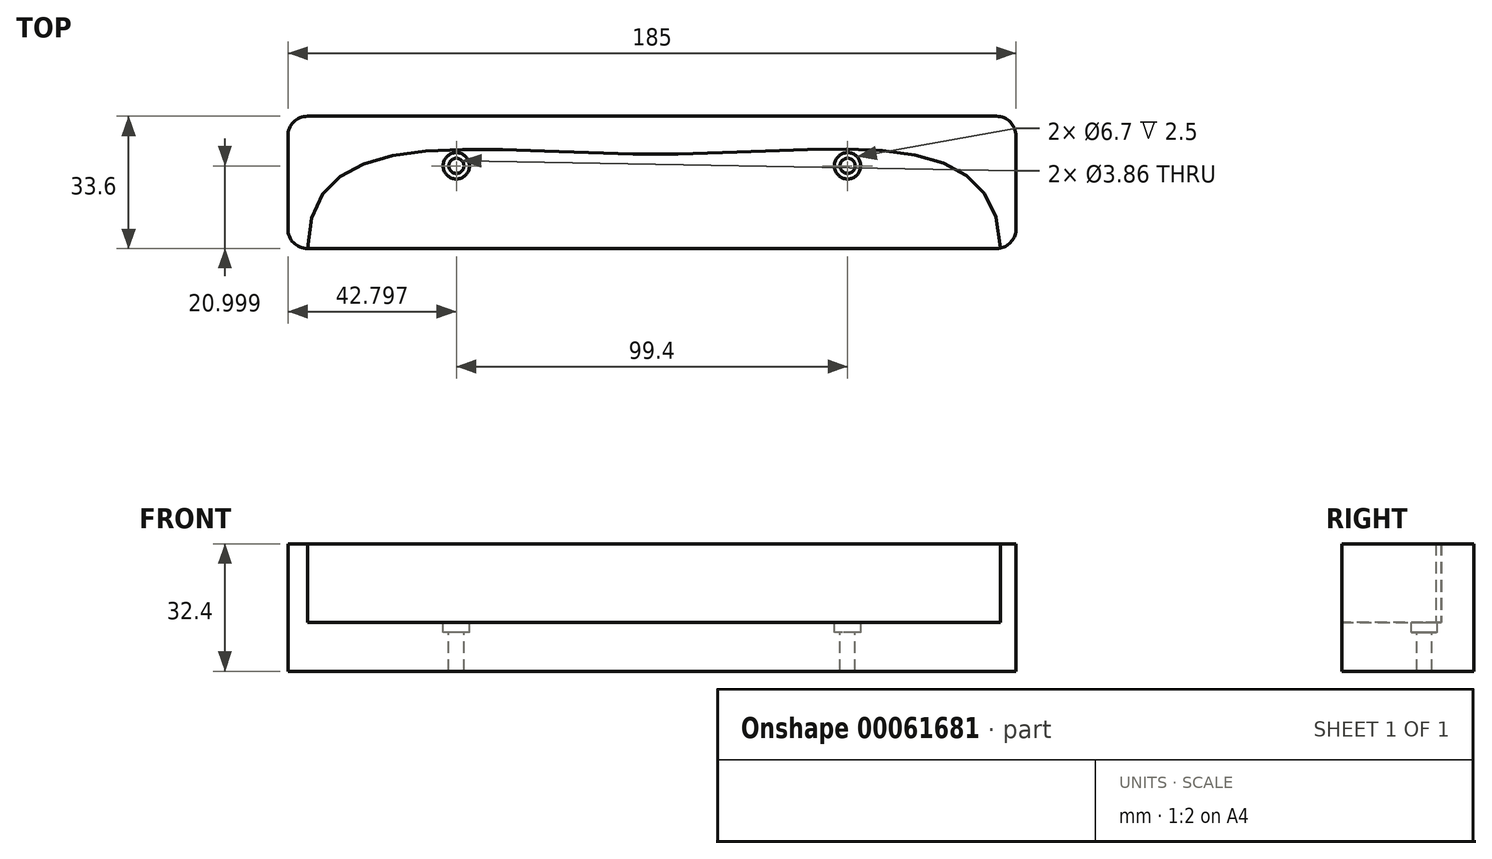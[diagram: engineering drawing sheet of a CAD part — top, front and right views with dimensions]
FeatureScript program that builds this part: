
annotation { "Feature Type Name" : "Feature", "Feature Type Description" : "" }
export const myFeature = defineFeature(function(context is Context, id is Id, definition is map)
    precondition{}
    {
        {
            var Q0;
            Q0=qCreatedBy(makeId("Top.planeOp"),FACE);
            var sketch = newSketch(context, id + "F0", { "sketchPlane" : qUnion([Q0])});
            skLineSegment(sketch, "E0.bottom", {"start": v(-89.36, -7.5) * mm, "end": v(85.64, -7.5) * mm});
            skLineSegment(sketch, "E0.top", {"start": v(-89.36, -41.1) * mm, "end": v(85.64, -41.1) * mm});
            skLineSegment(sketch, "E0.left", {"start": v(-94.36, -12.5) * mm, "end": v(-94.36, -36.1) * mm});
            skLineSegment(sketch, "E0.right", {"start": v(90.64, -12.5) * mm, "end": v(90.64, -36.1) * mm});
            skPoint(sketch, "E1.visualSharp", {"position": v(-94.36, -7.5) * mm});
            skArc(sketch, "E1.filletArc", {"start": v(-89.36, -7.5) * mm, "mid": v(-92.9, -8.97) * mm, "end": v(-94.36, -12.5) * mm});
            skPoint(sketch, "E2.visualSharp", {"position": v(-94.36, -41.1) * mm});
            skArc(sketch, "E2.filletArc", {"start": v(-94.36, -36.1) * mm, "mid": v(-92.9, -39.64) * mm, "end": v(-89.36, -41.1) * mm});
            skPoint(sketch, "E3.visualSharp", {"position": v(90.64, -41.1) * mm});
            skArc(sketch, "E3.filletArc", {"start": v(85.64, -41.1) * mm, "mid": v(89.17, -39.64) * mm, "end": v(90.64, -36.1) * mm});
            skPoint(sketch, "E4.visualSharp", {"position": v(90.64, -7.5) * mm});
            skArc(sketch, "E4.filletArc", {"start": v(90.64, -12.5) * mm, "mid": v(89.17, -8.97) * mm, "end": v(85.64, -7.5) * mm});
            skFitSpline(sketch, "E5", {"points": [v(-89.36, -41.1) * mm, v(0, -18.1) * mm, v(85.64, -41.1) * mm], "startDerivative": vector(177.84, 38.38) * mm, "endDerivative": vector(172.14, -38.64) * mm});
            skSolve(sketch);
        }
        {
            var Q0;
            {var subQ6=sQuery(id+"F0.wireOp",EDGE,"E0.left");Q0=makeQuery(id+"F0.imprint","IMPRINT",FACE,{"disambiguationData":[TD([[makeQuery(id+"F0.imprint","IMPRINT",EDGE,{"derivedFrom":subQ6}),1.0]])]});}
            var Q1;
            {var subQ0=sQuery(id+"F0.wireOp",EDGE,"E2.filletArc");var subQ1=sQuery(id+"F0.wireOp",EDGE,"E0.top");var subQ2=makeQuery(id+"F0.imprint","INTERSECT",VERTEX,{"derivedFrom":[subQ1,subQ0]});Q1=makeQuery(id+"F0.imprint","IMPRINT",FACE,{"disambiguationData":[TD([[makeQuery(id+"F0.imprint","IMPRINT",EDGE,{"disambiguationData":[TD([[subQ2,-1.0]])],"derivedFrom":subQ1}),1.0]])]});}
            var Q2;
            {var subQ5=sQuery(id+"F0.wireOp",EDGE,"DiWK0a0K-p0Ve-xPCM-Xpb8-uTkeJafHcErU");Q2=makeQuery(id+"F0.imprint","IMPRINT",FACE,{"disambiguationData":[TD([[makeQuery(id+"F0.imprint","IMPRINT",EDGE,{"derivedFrom":subQ5}),1.0]])]});}
            var Q3;
            {var subQ0=sQuery(id+"F0.wireOp",EDGE,"XpN96RJf-h1wa-usSg-oxlj-EXDZ94Ahnvhv");var subQ1=sQuery(id+"F0.wireOp",EDGE,"E0.top");var subQ2=makeQuery(id+"F0.imprint","INTERSECT",VERTEX,{"derivedFrom":[subQ1,subQ0]});Q3=makeQuery(id+"F0.imprint","IMPRINT",FACE,{"disambiguationData":[TD([[makeQuery(id+"F0.imprint","IMPRINT",EDGE,{"disambiguationData":[TD([[subQ2,1.0]])],"derivedFrom":subQ1}),1.0]])]});}
            var Q4;
            {var subQ5=sQuery(id+"F0.wireOp",EDGE,"Qj6dQj5D-QQnR-hAFS-0dMR-JZPYQxWabMse");Q4=makeQuery(id+"F0.imprint","IMPRINT",FACE,{"disambiguationData":[TD([[makeQuery(id+"F0.imprint","IMPRINT",EDGE,{"derivedFrom":subQ5}),-1.0]])]});}
            var Q5;
            {var subQ9=sQuery(id+"F0.wireOp",EDGE,"E0.right");Q5=makeQuery(id+"F0.imprint","IMPRINT",FACE,{"disambiguationData":[TD([[makeQuery(id+"F0.imprint","IMPRINT",EDGE,{"derivedFrom":subQ9}),-1.0]])]});}
            var Q6;
            {var subQ0=sQuery(id+"F0.wireOp",EDGE,"E3.filletArc");var subQ1=sQuery(id+"F0.wireOp",EDGE,"E0.top");var subQ2=makeQuery(id+"F0.imprint","INTERSECT",VERTEX,{"derivedFrom":[subQ1,subQ0]});Q6=makeQuery(id+"F0.imprint","IMPRINT",FACE,{"disambiguationData":[TD([[makeQuery(id+"F0.imprint","IMPRINT",EDGE,{"disambiguationData":[TD([[subQ2,1.0]])],"derivedFrom":subQ1}),1.0]])]});}
            var Q7;
            {var subQ0=sQuery(id+"F0.wireOp",EDGE,"8f524986-9a2f-477d-a438-1098895b14b8");var subQ1=sQuery(id+"F0.wireOp",EDGE,"q3M1eQDT-CZSL-Hfhw-1e6b-vYKe8UV4ZBwo");var subQ2=makeQuery(id+"F0.imprint","INTERSECT",VERTEX,{"disambiguationData":[OD(0.0)],"derivedFrom":[subQ1,subQ0]});Q7=makeQuery(id+"F0.imprint","IMPRINT",FACE,{"disambiguationData":[TD([[makeQuery(id+"F0.imprint","IMPRINT",EDGE,{"disambiguationData":[TD([[subQ2,-1.0]])],"derivedFrom":subQ1}),1.0]])]});}
            var Q8;
            {var subQ0=sQuery(id+"F0.wireOp",EDGE,"f629a123-b092-4783-abd5-7fa05e799837");var subQ1=sQuery(id+"F0.wireOp",EDGE,"q3M1eQDT-CZSL-Hfhw-1e6b-vYKe8UV4ZBwo");var subQ2=makeQuery(id+"F0.imprint","INTERSECT",VERTEX,{"disambiguationData":[OD(0.0)],"derivedFrom":[subQ1,subQ0]});Q8=makeQuery(id+"F0.imprint","IMPRINT",FACE,{"disambiguationData":[TD([[makeQuery(id+"F0.imprint","IMPRINT",EDGE,{"disambiguationData":[TD([[subQ2,-1.0]])],"derivedFrom":subQ1}),1.0]])]});}
            var Q9;
            {var subQ0=sQuery(id+"F0.wireOp",EDGE,"f629a123-b092-4783-abd5-7fa05e799837");var subQ1=sQuery(id+"F0.wireOp",EDGE,"q3M1eQDT-CZSL-Hfhw-1e6b-vYKe8UV4ZBwo");var subQ2=makeQuery(id+"F0.imprint","INTERSECT",VERTEX,{"disambiguationData":[OD(0.0)],"derivedFrom":[subQ1,subQ0]});Q9=makeQuery(id+"F0.imprint","IMPRINT",FACE,{"disambiguationData":[TD([[makeQuery(id+"F0.imprint","IMPRINT",EDGE,{"disambiguationData":[TD([[subQ2,-1.0]])],"derivedFrom":subQ1}),-1.0]])]});}
            var Q10;
            {var subQ0=sQuery(id+"F0.wireOp",EDGE,"8f524986-9a2f-477d-a438-1098895b14b8");var subQ1=sQuery(id+"F0.wireOp",EDGE,"q3M1eQDT-CZSL-Hfhw-1e6b-vYKe8UV4ZBwo");var subQ2=makeQuery(id+"F0.imprint","INTERSECT",VERTEX,{"disambiguationData":[OD(0.0)],"derivedFrom":[subQ1,subQ0]});Q10=makeQuery(id+"F0.imprint","IMPRINT",FACE,{"disambiguationData":[TD([[makeQuery(id+"F0.imprint","IMPRINT",EDGE,{"disambiguationData":[TD([[subQ2,-1.0]])],"derivedFrom":subQ1}),-1.0]])]});}
            var Q11;
            {var subQ0=sQuery(id+"F0.wireOp",EDGE,"e7c36ffa-8dd1-4ad2-a08c-114cf6db0365");var subQ1=sQuery(id+"F0.wireOp",EDGE,"NGp6TUnh-2WYz-SvJ6-BtMD-nmsAgSWZyCNH");var subQ2=makeQuery(id+"F0.imprint","INTERSECT",VERTEX,{"disambiguationData":[OD(0.0)],"derivedFrom":[subQ1,subQ0]});Q11=makeQuery(id+"F0.imprint","IMPRINT",FACE,{"disambiguationData":[TD([[makeQuery(id+"F0.imprint","IMPRINT",EDGE,{"disambiguationData":[TD([[subQ2,-1.0]])],"derivedFrom":subQ1}),1.0]])]});}
            var Q12;
            {var subQ0=sQuery(id+"F0.wireOp",EDGE,"e7c36ffa-8dd1-4ad2-a08c-114cf6db0365");var subQ1=sQuery(id+"F0.wireOp",EDGE,"NGp6TUnh-2WYz-SvJ6-BtMD-nmsAgSWZyCNH");var subQ2=makeQuery(id+"F0.imprint","INTERSECT",VERTEX,{"disambiguationData":[OD(0.0)],"derivedFrom":[subQ1,subQ0]});Q12=makeQuery(id+"F0.imprint","IMPRINT",FACE,{"disambiguationData":[TD([[makeQuery(id+"F0.imprint","IMPRINT",EDGE,{"disambiguationData":[TD([[subQ2,-1.0]])],"derivedFrom":subQ1}),-1.0]])]});}
            var Q13;
            {var subQ0=sQuery(id+"F0.wireOp",EDGE,"635bec6d-890f-4d85-b6bb-3d27c9027523");var subQ1=sQuery(id+"F0.wireOp",EDGE,"NGp6TUnh-2WYz-SvJ6-BtMD-nmsAgSWZyCNH");var subQ2=makeQuery(id+"F0.imprint","INTERSECT",VERTEX,{"disambiguationData":[OD(0.0)],"derivedFrom":[subQ1,subQ0]});Q13=makeQuery(id+"F0.imprint","IMPRINT",FACE,{"disambiguationData":[TD([[makeQuery(id+"F0.imprint","IMPRINT",EDGE,{"disambiguationData":[TD([[subQ2,-1.0]])],"derivedFrom":subQ1}),-1.0]])]});}
            var Q14;
            {var subQ0=sQuery(id+"F0.wireOp",EDGE,"635bec6d-890f-4d85-b6bb-3d27c9027523");var subQ1=sQuery(id+"F0.wireOp",EDGE,"NGp6TUnh-2WYz-SvJ6-BtMD-nmsAgSWZyCNH");var subQ2=makeQuery(id+"F0.imprint","INTERSECT",VERTEX,{"disambiguationData":[OD(0.0)],"derivedFrom":[subQ1,subQ0]});Q14=makeQuery(id+"F0.imprint","IMPRINT",FACE,{"disambiguationData":[TD([[makeQuery(id+"F0.imprint","IMPRINT",EDGE,{"disambiguationData":[TD([[subQ2,-1.0]])],"derivedFrom":subQ1}),1.0]])]});}
            var Q15;
            {var subQ0=sQuery(id+"F0.wireOp",EDGE,"XpN96RJf-h1wa-usSg-oxlj-EXDZ94Ahnvhv");var subQ1=sQuery(id+"F0.wireOp",EDGE,"E0.top");var subQ2=makeQuery(id+"F0.imprint","INTERSECT",VERTEX,{"derivedFrom":[subQ1,subQ0]});Q15=makeQuery(id+"F0.imprint","IMPRINT",FACE,{"disambiguationData":[TD([[makeQuery(id+"F0.imprint","IMPRINT",EDGE,{"disambiguationData":[TD([[subQ2,-1.0]])],"derivedFrom":subQ1}),1.0]])]});}
            extrude(context, id + "F1", {"entities" : qUnion([Q0, Q1, Q2, Q3, Q4, Q5, Q6, Q7, Q8, Q9, Q10, Q11, Q12, Q13, Q14, Q15]), "depth" : 32.4 * mm});
        }
        {
            var Q0;
            Q0=makeQuery(id+"F1.opExtrude","CAP_FACE",FACE,{"disambiguationData":[OSD([sQuery(id+"F0.wireOp",EDGE,"E0.bottom"),sQuery(id+"F0.wireOp",EDGE,"E0.top"),sQuery(id+"F0.wireOp",EDGE,"E0.left"),sQuery(id+"F0.wireOp",EDGE,"E0.right"),sQuery(id+"F0.wireOp",EDGE,"E1.filletArc"),sQuery(id+"F0.wireOp",EDGE,"E2.filletArc"),sQuery(id+"F0.wireOp",EDGE,"E3.filletArc"),sQuery(id+"F0.wireOp",EDGE,"E4.filletArc")])],"isStart":false});
            var sketch = newSketch(context, id + "F2", { "sketchPlane" : qUnion([Q0])});
            skFitSpline(sketch, "E6", {"points": [v(-89.36, -41.1) * mm, v(0, -17.14) * mm, v(86.67, -41) * mm], "startDerivative": vector(0, 200.16) * mm, "endDerivative": vector(6.27, -202.4) * mm});
            skSolve(sketch);
        }
        {
            var Q0;
            {var subQ0=sQuery(id+"F2.wireOp",EDGE,"E6");Q0=makeQuery(id+"F2.imprint","IMPRINT",FACE,{"disambiguationData":[TD([[makeQuery(id+"F2.imprint","IMPRINT",EDGE,{"derivedFrom":subQ0}),-1.0]])]});}
            extrude(context, id + "F3", {"entities" : qUnion([Q0]), "operationType" : NewBodyOperationType.REMOVE, "oppositeDirection" : true, "depth" : 20 * mm});
        }
        {
            var Q0;
            Q0=makeQuery(id+"F3.boolean.opBoolean","COPY",FACE,{"derivedFrom":makeQuery(id+"F3.opExtrude","CAP_FACE",FACE,{"disambiguationData":[OSD([sQuery(id+"F0.wireOp",EDGE,"E0.top"),sQuery(id+"F0.wireOp",EDGE,"E3.filletArc"),sQuery(id+"F2.wireOp",EDGE,"E6")])],"isStart":false})});
            var sketch = newSketch(context, id + "F4", { "sketchPlane" : qUnion([Q0])});
            skLineSegment(sketch, "E7", {"start": v(-1.86, -41.1) * mm, "end": v(-1.86, -20.1) * mm});
            skLineSegment(sketch, "E8", {"start": v(-1.86, -20.1) * mm, "end": v(-51.56, -20.1) * mm});
            skLineSegment(sketch, "E9", {"start": v(-1.86, -20.1) * mm, "end": v(47.84, -20.1) * mm});
            skCircle(sketch, "E10", {"center": v(-51.56, -20.1) * mm, "radius": 3.35 * mm});
            skCircle(sketch, "E11", {"center": v(47.84, -20.1) * mm, "radius": 3.35 * mm});
            skSolve(sketch);
        }
        {
            var Q0;
            Q0=makeQuery(id+"F4.imprint","IMPRINT",FACE,{"disambiguationData":[TD([[makeQuery(id+"F4.imprint","IMPRINT",EDGE,{"derivedFrom":sQuery(id+"F4.wireOp",EDGE,"E10")}),1.0]])]});
            var Q1;
            Q1=makeQuery(id+"F4.imprint","IMPRINT",FACE,{"disambiguationData":[TD([[makeQuery(id+"F4.imprint","IMPRINT",EDGE,{"derivedFrom":sQuery(id+"F4.wireOp",EDGE,"E11")}),1.0]])]});
            extrude(context, id + "F5", {"entities" : qUnion([Q0, Q1]), "operationType" : NewBodyOperationType.REMOVE, "oppositeDirection" : true, "depth" : 2.5 * mm});
        }
        {
            var Q0;
            Q0=makeQuery(id+"F5.boolean.opBoolean","COPY",FACE,{"derivedFrom":makeQuery(id+"F5.opExtrude","CAP_FACE",FACE,{"disambiguationData":[OSD([sQuery(id+"F4.wireOp",EDGE,"E10")])],"isStart":false})});
            var sketch = newSketch(context, id + "F6", { "sketchPlane" : qUnion([Q0])});
            skCircle(sketch, "E12", {"center": v(-51.56, -20.1) * mm, "radius": 1.93 * mm});
            skSolve(sketch);
        }
        {
            var Q0;
            Q0=makeQuery(id+"F6.imprint","IMPRINT",FACE,{"disambiguationData":[TD([[makeQuery(id+"F6.imprint","IMPRINT",EDGE,{"derivedFrom":sQuery(id+"F6.wireOp",EDGE,"E12")}),1.0]])]});
            extrude(context, id + "F7", {"entities" : qUnion([Q0]), "operationType" : NewBodyOperationType.REMOVE, "oppositeDirection" : true, "depth" : 25 * mm});
        }
        {
            var Q0;
            Q0=makeQuery(id+"F5.boolean.opBoolean","COPY",FACE,{"derivedFrom":makeQuery(id+"F5.opExtrude","CAP_FACE",FACE,{"disambiguationData":[OSD([sQuery(id+"F4.wireOp",EDGE,"E11")])],"isStart":false})});
            var sketch = newSketch(context, id + "F8", { "sketchPlane" : qUnion([Q0])});
            skCircle(sketch, "E13", {"center": v(47.84, -20.1) * mm, "radius": 1.93 * mm});
            skSolve(sketch);
        }
        {
            var Q0;
            Q0 = qSketchRegion(id + "F8", true);
            extrude(context, id + "F9", {"entities" : qUnion([Q0]), "operationType" : NewBodyOperationType.REMOVE, "oppositeDirection" : true, "depth" : 25 * mm});
        }
    });
